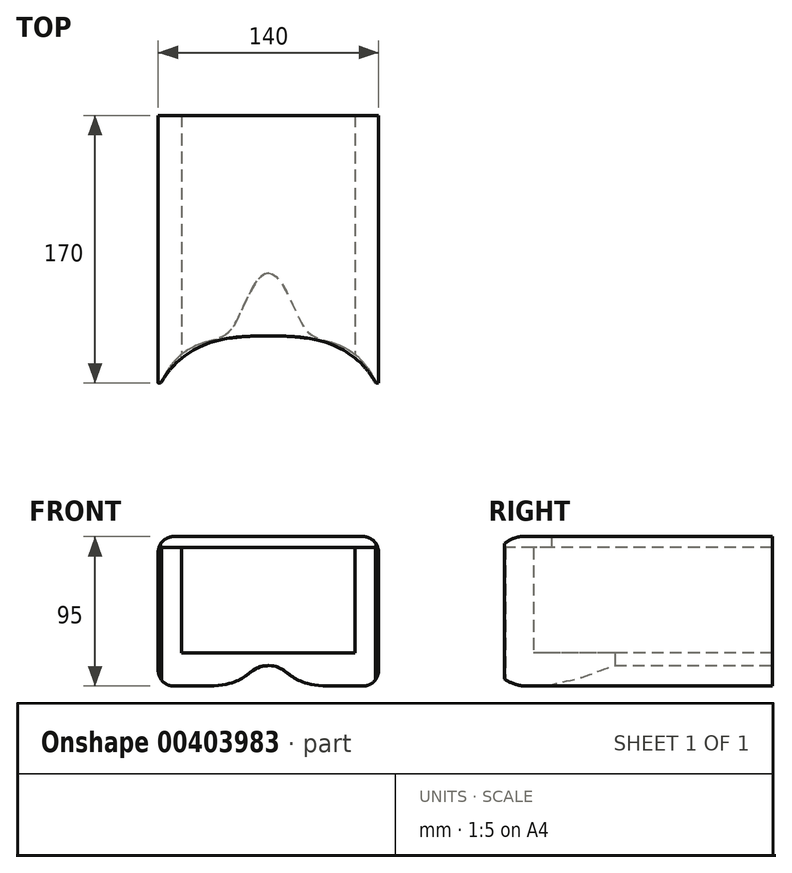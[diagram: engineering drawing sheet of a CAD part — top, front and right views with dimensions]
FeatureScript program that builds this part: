
annotation { "Feature Type Name" : "Feature", "Feature Type Description" : "" }
export const myFeature = defineFeature(function(context is Context, id is Id, definition is map)
    precondition{}
    {
        {
            var Q0;
            Q0=qCreatedBy(makeId("Top.planeOp"),FACE);
            var sketch = newSketch(context, id + "F0", { "sketchPlane" : qUnion([Q0])});
            skLineSegment(sketch, "E0.bottom", {"start": v(70, 85) * mm, "end": v(-70, 85) * mm});
            skLineSegment(sketch, "E0.top", {"start": v(70, -85) * mm, "end": v(-70, -85) * mm});
            skLineSegment(sketch, "E0.left", {"start": v(70, 85) * mm, "end": v(70, -85) * mm});
            skLineSegment(sketch, "E0.right", {"start": v(-70, 85) * mm, "end": v(-70, -85) * mm});
            skPoint(sketch, "E0.middle", {"position": v(0, 0) * mm});
            skSolve(sketch);
        }
        {
            var Q0;
            Q0 = qSketchRegion(id + "F0", true);
            extrude(context, id + "F1", {"entities" : qUnion([Q0]), "depth" : 95 * mm});
        }
        {
            var Q0;
            Q0=makeQuery(id+"F1.opExtrude","SWEPT_FACE",FACE,{"disambiguationData":[OSD([sQuery(id+"F0.wireOp",EDGE,"E0.top")])]});
            var sketch = newSketch(context, id + "F2", { "sketchPlane" : qUnion([Q0])});
            skLineSegment(sketch, "E1.bottom", {"start": v(-55, 88) * mm, "end": v(55, 88) * mm});
            skLineSegment(sketch, "E1.top", {"start": v(-55, 21) * mm, "end": v(55, 21) * mm});
            skLineSegment(sketch, "E1.left", {"start": v(-55, 88) * mm, "end": v(-55, 21) * mm});
            skLineSegment(sketch, "E1.right", {"start": v(55, 88) * mm, "end": v(55, 21) * mm});
            skSolve(sketch);
        }
        {
            var Q0;
            Q0 = qSketchRegion(id + "F2", true);
            extrude(context, id + "F3", {"entities" : qUnion([Q0]), "operationType" : NewBodyOperationType.REMOVE, "endBound" : BoundingType.THROUGH_ALL, "oppositeDirection" : true, "depth" : 25 * mm});
        }
        {
            var Q0;
            Q0=makeQuery(id+"F1.opExtrude","CAP_FACE",FACE,{"disambiguationData":[OSD([sQuery(id+"F0.wireOp",EDGE,"E0.bottom"),sQuery(id+"F0.wireOp",EDGE,"E0.top"),sQuery(id+"F0.wireOp",EDGE,"E0.left"),sQuery(id+"F0.wireOp",EDGE,"E0.right")])],"isStart":true});
            var sketch = newSketch(context, id + "F4", { "sketchPlane" : qUnion([Q0])});
            skLineSegment(sketch, "E2", {"start": v(0, -85) * mm, "end": v(0, 85) * mm, "construction": true});
            skLineSegment(sketch, "E3.1.0.0", {"start": v(-10, -85) * mm, "end": v(-10, 85) * mm, "construction": true});
            skLineSegment(sketch, "E3.2.0.0", {"start": v(-20, -85) * mm, "end": v(-20, 85) * mm, "construction": true});
            skLineSegment(sketch, "E3.3.0.0", {"start": v(-30, -85) * mm, "end": v(-30, 85) * mm, "construction": true});
            skLineSegment(sketch, "E3.4.0.0", {"start": v(-40, -85) * mm, "end": v(-40, 85) * mm, "construction": true});
            skLineSegment(sketch, "E3.5.0.0", {"start": v(-50, -85) * mm, "end": v(-50, 85) * mm, "construction": true});
            skLineSegment(sketch, "E3.6.0.0", {"start": v(-60, -85) * mm, "end": v(-60, 85) * mm, "construction": true});
            skLineSegment(sketch, "E3.direction1", {"start": v(0, -85) * mm, "end": v(-10, -85) * mm, "construction": true});
            skLineSegment(sketch, "E4.1.0.0", {"start": v(10, -85) * mm, "end": v(10, 85) * mm, "construction": true});
            skLineSegment(sketch, "E4.2.0.0", {"start": v(20, -85) * mm, "end": v(20, 85) * mm, "construction": true});
            skLineSegment(sketch, "E4.3.0.0", {"start": v(30, -85) * mm, "end": v(30, 85) * mm, "construction": true});
            skLineSegment(sketch, "E4.4.0.0", {"start": v(40, -85) * mm, "end": v(40, 85) * mm, "construction": true});
            skLineSegment(sketch, "E4.5.0.0", {"start": v(50, -85) * mm, "end": v(50, 85) * mm, "construction": true});
            skLineSegment(sketch, "E4.6.0.0", {"start": v(60, -85) * mm, "end": v(60, 85) * mm, "construction": true});
            skLineSegment(sketch, "E4.direction1", {"start": v(0, -85) * mm, "end": v(10, -85) * mm, "construction": true});
            skLineSegment(sketch, "E5", {"start": v(70, 15) * mm, "end": v(-70, 15) * mm, "construction": true});
            skLineSegment(sketch, "E6.0.1.0", {"start": v(70, 25) * mm, "end": v(-70, 25) * mm, "construction": true});
            skLineSegment(sketch, "E6.0.2.0", {"start": v(70, 35) * mm, "end": v(-70, 35) * mm, "construction": true});
            skLineSegment(sketch, "E6.0.3.0", {"start": v(70, 45) * mm, "end": v(-70, 45) * mm, "construction": true});
            skLineSegment(sketch, "E6.0.4.0", {"start": v(70, 55) * mm, "end": v(-70, 55) * mm, "construction": true});
            skLineSegment(sketch, "E6.0.5.0", {"start": v(70, 65) * mm, "end": v(-70, 65) * mm, "construction": true});
            skLineSegment(sketch, "E6.0.6.0", {"start": v(70, 75) * mm, "end": v(-70, 75) * mm, "construction": true});
            skLineSegment(sketch, "E6.1.0.0", {"start": v(95, 15) * mm, "end": v(-45, 15) * mm, "construction": true});
            skLineSegment(sketch, "E6.1.1.0", {"start": v(95, 25) * mm, "end": v(-45, 25) * mm, "construction": true});
            skLineSegment(sketch, "E6.1.2.0", {"start": v(95, 35) * mm, "end": v(-45, 35) * mm, "construction": true});
            skLineSegment(sketch, "E6.1.3.0", {"start": v(95, 45) * mm, "end": v(-45, 45) * mm, "construction": true});
            skLineSegment(sketch, "E6.1.4.0", {"start": v(95, 55) * mm, "end": v(-45, 55) * mm, "construction": true});
            skLineSegment(sketch, "E6.1.5.0", {"start": v(95, 65) * mm, "end": v(-45, 65) * mm, "construction": true});
            skLineSegment(sketch, "E6.1.6.0", {"start": v(95, 75) * mm, "end": v(-45, 75) * mm, "construction": true});
            skLineSegment(sketch, "E6.2.0.0", {"start": v(120, 15) * mm, "end": v(-20, 15) * mm, "construction": true});
            skLineSegment(sketch, "E6.2.1.0", {"start": v(120, 25) * mm, "end": v(-20, 25) * mm, "construction": true});
            skLineSegment(sketch, "E6.2.2.0", {"start": v(120, 35) * mm, "end": v(-20, 35) * mm, "construction": true});
            skLineSegment(sketch, "E6.2.3.0", {"start": v(120, 45) * mm, "end": v(-20, 45) * mm, "construction": true});
            skLineSegment(sketch, "E6.2.4.0", {"start": v(120, 55) * mm, "end": v(-20, 55) * mm, "construction": true});
            skLineSegment(sketch, "E6.2.5.0", {"start": v(120, 65) * mm, "end": v(-20, 65) * mm, "construction": true});
            skLineSegment(sketch, "E6.2.6.0", {"start": v(120, 75) * mm, "end": v(-20, 75) * mm, "construction": true});
            skLineSegment(sketch, "E6.direction1", {"start": v(-70, 15) * mm, "end": v(-45, 15) * mm, "construction": true});
            skLineSegment(sketch, "E6.direction2", {"start": v(-70, 15) * mm, "end": v(-70, 25) * mm, "construction": true});
            skFitSpline(sketch, "E7", {"points": [v(0, 15) * mm, v(20, 45) * mm, v(31.85, 56.6) * mm, v(68.26, 85) * mm], "startDerivative": vector(65.7, 0) * mm, "endDerivative": vector(77.5, 177.86) * mm});
            skFitSpline(sketch, "E8.MirrorCS", {"points": [v(0, 15) * mm, v(-20, 45) * mm, v(-31.85, 56.6) * mm, v(-68.26, 85) * mm], "startDerivative": vector(-65.7, 0) * mm, "endDerivative": vector(-77.5, 177.86) * mm});
            skLineSegment(sketch, "E9", {"start": v(68.26, 85) * mm, "end": v(-68.26, 85) * mm});
            skSolve(sketch);
        }
        {
            var Q0;
            Q0=makeQuery(id+"F4.imprint","IMPRINT",FACE,{"disambiguationData":[TD([[makeQuery(id+"F4.imprint","IMPRINT",EDGE,{"derivedFrom":sQuery(id+"F4.wireOp",EDGE,"E7")}),1.0]])]});
            extrude(context, id + "F5", {"entities" : qUnion([Q0]), "operationType" : NewBodyOperationType.REMOVE, "oppositeDirection" : true, "depth" : 88 * mm});
        }
        {
            var Q0;
            Q0=makeQuery(id+"F1.opExtrude","CAP_FACE",FACE,{"disambiguationData":[OSD([sQuery(id+"F0.wireOp",EDGE,"E0.bottom"),sQuery(id+"F0.wireOp",EDGE,"E0.top"),sQuery(id+"F0.wireOp",EDGE,"E0.left"),sQuery(id+"F0.wireOp",EDGE,"E0.right")])],"isStart":false});
            var sketch = newSketch(context, id + "F6", { "sketchPlane" : qUnion([Q0])});
            skLineSegment(sketch, "E10", {"start": v(-70, -55) * mm, "end": v(70, -55) * mm, "construction": true});
            skLineSegment(sketch, "E11", {"start": v(68.3, -85) * mm, "end": v(68.3, -55) * mm, "construction": true});
            skLineSegment(sketch, "E12", {"start": v(-68.36, -85) * mm, "end": v(-68.36, -55) * mm, "construction": true});
            skLineSegment(sketch, "E13", {"start": v(0, -85) * mm, "end": v(0, -55) * mm, "construction": true});
            skFitSpline(sketch, "E14", {"points": [v(0, -55) * mm, v(-47.97, -64.27) * mm, v(-68.36, -85) * mm], "startDerivative": vector(-134.93, 0) * mm, "endDerivative": vector(-37.97, -66.04) * mm});
            skFitSpline(sketch, "E15.MirrorCS", {"points": [v(0, -55) * mm, v(47.97, -64.27) * mm, v(68.36, -85) * mm], "startDerivative": vector(134.93, 0) * mm, "endDerivative": vector(37.97, -66.04) * mm});
            skLineSegment(sketch, "E16", {"start": v(-68.36, -85) * mm, "end": v(68.36, -85) * mm});
            skSolve(sketch);
        }
        {
            var Q0;
            Q0=makeQuery(id+"F6.imprint","IMPRINT",FACE,{"disambiguationData":[TD([[makeQuery(id+"F6.imprint","IMPRINT",EDGE,{"derivedFrom":sQuery(id+"F6.wireOp",EDGE,"E14")}),1.0]])]});
            extrude(context, id + "F7", {"entities" : qUnion([Q0]), "operationType" : NewBodyOperationType.REMOVE, "endBound" : BoundingType.UP_TO_NEXT, "oppositeDirection" : true, "depth" : 25 * mm});
        }
        {
            var Q0;
            Q0=makeQuery(id+"F1.opExtrude","CAP_EDGE",EDGE,{"disambiguationData":[OSD([sQuery(id+"F0.wireOp",EDGE,"E0.left")])],"isStart":false});
            var Q1;
            Q1=makeQuery(id+"F1.opExtrude","CAP_EDGE",EDGE,{"disambiguationData":[OSD([sQuery(id+"F0.wireOp",EDGE,"E0.left")])],"isStart":true});
            var Q2;
            Q2=makeQuery(id+"F1.opExtrude","CAP_EDGE",EDGE,{"disambiguationData":[OSD([sQuery(id+"F0.wireOp",EDGE,"E0.right")])],"isStart":true});
            var Q3;
            Q3=makeQuery(id+"F1.opExtrude","CAP_EDGE",EDGE,{"disambiguationData":[OSD([sQuery(id+"F0.wireOp",EDGE,"E0.right")])],"isStart":false});
            fillet(context, id + "F8", {"entities" : qUnion([Q0, Q1, Q2, Q3]), "radius" : 10 * mm, "tangentPropagation" : true, "allowEdgeOverflow" : false});
        }
        {
            var Q0;
            Q0=makeQuery(id+"F1.opExtrude","SWEPT_FACE",FACE,{"disambiguationData":[OSD([sQuery(id+"F0.wireOp",EDGE,"E0.bottom")])]});
            var sketch = newSketch(context, id + "F9", { "sketchPlane" : qUnion([Q0])});
            skLineSegment(sketch, "E17", {"start": v(0, 21) * mm, "end": v(0, 0) * mm, "construction": true});
            skLineSegment(sketch, "E18", {"start": v(-70, 13) * mm, "end": v(70, 13) * mm, "construction": true});
            skLineSegment(sketch, "E19", {"start": v(-40, 21) * mm, "end": v(-40, 0) * mm, "construction": true});
            skFitSpline(sketch, "E20", {"points": [v(0, 13) * mm, v(-40, 0) * mm], "startDerivative": vector(-42.54, 0) * mm, "endDerivative": vector(-86.95, 0) * mm});
            skFitSpline(sketch, "E21.MirrorCS", {"points": [v(0, 13) * mm, v(40, 0) * mm], "startDerivative": vector(42.54, 0) * mm, "endDerivative": vector(86.95, 0) * mm});
            skLineSegment(sketch, "E22", {"start": v(40, 0) * mm, "end": v(-40, 0) * mm});
            skSolve(sketch);
        }
        {
            var Q0;
            Q0=makeQuery(id+"F9.imprint","IMPRINT",FACE,{"disambiguationData":[TD([[makeQuery(id+"F9.imprint","IMPRINT",EDGE,{"derivedFrom":sQuery(id+"F9.wireOp",EDGE,"E20")}),1.0]])]});
            extrude(context, id + "F10", {"entities" : qUnion([Q0]), "operationType" : NewBodyOperationType.REMOVE, "endBound" : BoundingType.THROUGH_ALL, "oppositeDirection" : true, "depth" : 25 * mm});
        }
    });
